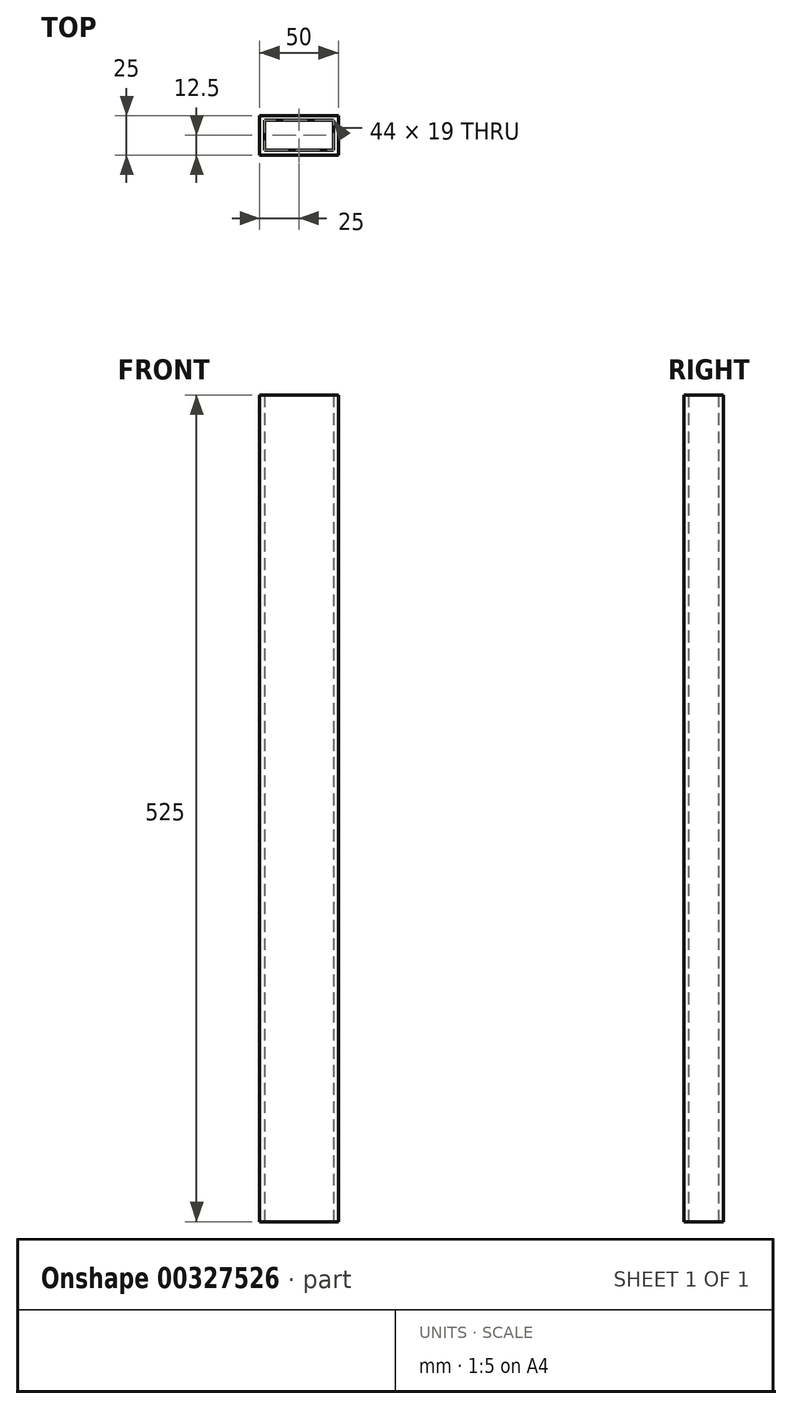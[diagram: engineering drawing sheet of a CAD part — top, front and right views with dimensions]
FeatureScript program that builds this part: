
annotation { "Feature Type Name" : "Feature", "Feature Type Description" : "" }
export const myFeature = defineFeature(function(context is Context, id is Id, definition is map)
    precondition{}
    {
        {
            var Q0;
            Q0=qCreatedBy(makeId("Top.planeOp"),FACE);
            var sketch = newSketch(context, id + "F0", { "sketchPlane" : qUnion([Q0])});
            skLineSegment(sketch, "E0.bottom", {"start": v(-25, -12.5) * mm, "end": v(25, -12.5) * mm});
            skLineSegment(sketch, "E0.top", {"start": v(-25, 12.5) * mm, "end": v(25, 12.5) * mm});
            skLineSegment(sketch, "E0.left", {"start": v(-25, -12.5) * mm, "end": v(-25, 12.5) * mm});
            skLineSegment(sketch, "E0.right", {"start": v(25, -12.5) * mm, "end": v(25, 12.5) * mm});
            skPoint(sketch, "E0.middle", {"position": v(0, 0) * mm});
            skLineSegment(sketch, "E1.bottom", {"start": v(-22, -9.5) * mm, "end": v(22, -9.5) * mm});
            skLineSegment(sketch, "E1.top", {"start": v(-22, 9.5) * mm, "end": v(22, 9.5) * mm});
            skLineSegment(sketch, "E1.left", {"start": v(-22, -9.5) * mm, "end": v(-22, 9.5) * mm});
            skLineSegment(sketch, "E1.right", {"start": v(22, -9.5) * mm, "end": v(22, 9.5) * mm});
            skSolve(sketch);
        }
        {
            var Q0;
            Q0=makeQuery(id+"F0.imprint","IMPRINT",FACE,{"disambiguationData":[TD([[makeQuery(id+"F0.imprint","IMPRINT",EDGE,{"derivedFrom":sQuery(id+"F0.wireOp",EDGE,"E0.bottom")}),1.0]])]});
            extrude(context, id + "F1", {"entities" : qUnion([Q0]), "depth" : 525 * mm, "symmetric" : true});
        }
    });
